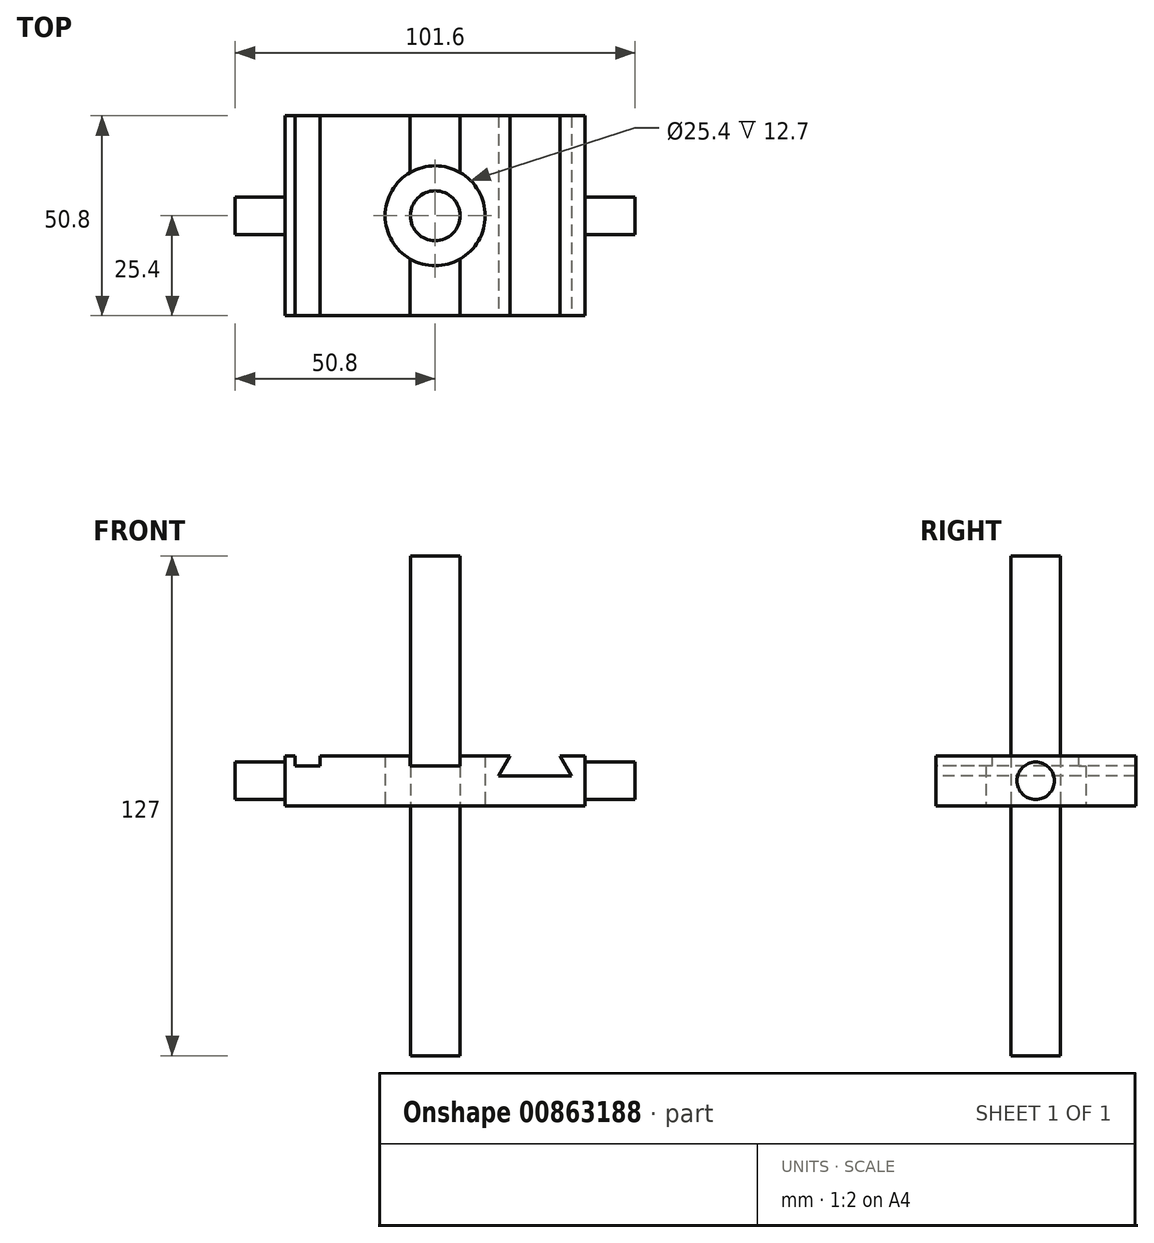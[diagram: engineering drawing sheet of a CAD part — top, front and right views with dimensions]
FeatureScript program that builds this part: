
annotation { "Feature Type Name" : "Feature", "Feature Type Description" : "" }
export const myFeature = defineFeature(function(context is Context, id is Id, definition is map)
    precondition{}
    {
        {
            var Q0;
            Q0=qCreatedBy(makeId("Top.planeOp"),FACE);
            var sketch = newSketch(context, id + "F0", { "sketchPlane" : qUnion([Q0])});
            skLineSegment(sketch, "E0.bottom", {"start": v(38.1, 25.4) * mm, "end": v(-38.1, 25.4) * mm});
            skLineSegment(sketch, "E0.top", {"start": v(38.1, -25.4) * mm, "end": v(-38.1, -25.4) * mm});
            skLineSegment(sketch, "E0.left", {"start": v(38.1, 25.4) * mm, "end": v(38.1, -25.4) * mm});
            skLineSegment(sketch, "E0.right", {"start": v(-38.1, 25.4) * mm, "end": v(-38.1, -25.4) * mm});
            skPoint(sketch, "E0.middle", {"position": v(0, 0) * mm});
            skCircle(sketch, "E1", {"center": v(0, 0) * mm, "radius": 12.7 * mm});
            skSolve(sketch);
        }
        {
            var Q0;
            Q0=makeQuery(id+"F0.imprint","IMPRINT",FACE,{"disambiguationData":[TD([[makeQuery(id+"F0.imprint","IMPRINT",EDGE,{"derivedFrom":sQuery(id+"F0.wireOp",EDGE,"E0.bottom")}),1.0]])]});
            extrude(context, id + "F1", {"entities" : qUnion([Q0]), "depth" : 12.7 * mm, "offsetDistance" : 25.4 * mm});
        }
        {
            var Q0;
            Q0=makeQuery(id+"F1.opExtrude","CAP_FACE",FACE,{"disambiguationData":[OSD([sQuery(id+"F0.wireOp",EDGE,"E0.bottom"),sQuery(id+"F0.wireOp",EDGE,"E0.top"),sQuery(id+"F0.wireOp",EDGE,"E0.left"),sQuery(id+"F0.wireOp",EDGE,"E0.right"),sQuery(id+"F0.wireOp",EDGE,"E1")])],"isStart":false});
            var sketch = newSketch(context, id + "F2", { "sketchPlane" : qUnion([Q0])});
            skLineSegment(sketch, "E2.bottom", {"start": v(-35.56, 25.4) * mm, "end": v(-29.21, 25.4) * mm});
            skLineSegment(sketch, "E2.top", {"start": v(-35.56, -25.4) * mm, "end": v(-29.21, -25.4) * mm});
            skLineSegment(sketch, "E2.left", {"start": v(-35.56, 25.4) * mm, "end": v(-35.56, -25.4) * mm});
            skLineSegment(sketch, "E2.right", {"start": v(-29.21, 25.4) * mm, "end": v(-29.21, -25.4) * mm});
            skLineSegment(sketch, "E3", {"start": v(-6.35, 25.4) * mm, "end": v(-6.35, -25.4) * mm});
            skLineSegment(sketch, "E4", {"start": v(-6.35, -25.4) * mm, "end": v(6.35, -25.4) * mm});
            skLineSegment(sketch, "E5", {"start": v(6.35, -25.4) * mm, "end": v(6.35, 25.4) * mm});
            skLineSegment(sketch, "E6", {"start": v(6.35, 25.4) * mm, "end": v(-6.35, 25.4) * mm});
            skPoint(sketch, "E7", {"position": v(0, 0) * mm});
            skLineSegment(sketch, "E8", {"start": v(0, 25.4) * mm, "end": v(0, -25.4) * mm, "construction": true});
            skSolve(sketch);
        }
        {
            var Q0;
            Q0=makeQuery(id+"F2.imprint","IMPRINT",FACE,{"disambiguationData":[TD([[makeQuery(id+"F2.imprint","IMPRINT",EDGE,{"derivedFrom":sQuery(id+"F2.wireOp",EDGE,"E2.bottom")}),1.0]])]});
            var Q1;
            {var subQ0=sQuery(id+"F2.wireOp",EDGE,"E6");Q1=makeQuery(id+"F2.imprint","IMPRINT",FACE,{"disambiguationData":[TD([[makeQuery(id+"F2.imprint","IMPRINT",EDGE,{"derivedFrom":subQ0}),1.0]])]});}
            var Q2;
            {var subQ0=sQuery(id+"F2.wireOp",EDGE,"E4");Q2=makeQuery(id+"F2.imprint","IMPRINT",FACE,{"disambiguationData":[TD([[makeQuery(id+"F2.imprint","IMPRINT",EDGE,{"derivedFrom":subQ0}),-1.0]])]});}
            extrude(context, id + "F3", {"entities" : qUnion([Q0, Q1, Q2]), "operationType" : NewBodyOperationType.REMOVE, "oppositeDirection" : true, "depth" : 2.54 * mm, "offsetDistance" : 25.4 * mm});
        }
        {
            var Q0;
            Q0=makeQuery(id+"F1.opExtrude","SWEPT_FACE",FACE,{"disambiguationData":[OSD([sQuery(id+"F0.wireOp",EDGE,"E0.top")])]});
            var sketch = newSketch(context, id + "F4", { "sketchPlane" : qUnion([Q0])});
            skLineSegment(sketch, "E9", {"start": v(19.05, 12.7) * mm, "end": v(16.12, 7.62) * mm});
            skLineSegment(sketch, "E10", {"start": v(16.12, 7.62) * mm, "end": v(34.68, 7.62) * mm});
            skLineSegment(sketch, "E11", {"start": v(34.68, 7.62) * mm, "end": v(31.75, 12.7) * mm});
            skLineSegment(sketch, "E12", {"start": v(19.05, 12.7) * mm, "end": v(31.75, 12.7) * mm, "construction": true});
            skLineSegment(sketch, "E13", {"start": v(25.4, 12.7) * mm, "end": v(25.4, 7.62) * mm, "construction": true});
            skSolve(sketch);
        }
        {
            var Q0;
            {var subQ0=sQuery(id+"F4.wireOp",EDGE,"E9");Q0=makeQuery(id+"F4.imprint","IMPRINT",FACE,{"disambiguationData":[TD([[makeQuery(id+"F4.imprint","IMPRINT",EDGE,{"derivedFrom":subQ0}),1.0]])]});}
            extrude(context, id + "F5", {"entities" : qUnion([Q0]), "operationType" : NewBodyOperationType.REMOVE, "endBound" : BoundingType.THROUGH_ALL, "oppositeDirection" : true, "depth" : 25.4 * mm, "offsetDistance" : 25.4 * mm});
        }
        {
            var Q0;
            Q0=makeQuery(id+"F1.opExtrude","SWEPT_FACE",FACE,{"disambiguationData":[OSD([sQuery(id+"F0.wireOp",EDGE,"E0.left")])]});
            var sketch = newSketch(context, id + "F6", { "sketchPlane" : qUnion([Q0])});
            skLineSegment(sketch, "E14", {"start": v(-25.4, 6.35) * mm, "end": v(25.4, 6.35) * mm, "construction": true});
            skLineSegment(sketch, "E15", {"start": v(0, 12.7) * mm, "end": v(0, 0) * mm, "construction": true});
            skCircle(sketch, "E16", {"center": v(0, 6.35) * mm, "radius": 4.76 * mm});
            skSolve(sketch);
        }
        {
            var Q0;
            Q0=makeQuery(id+"F6.imprint","IMPRINT",FACE,{"disambiguationData":[TD([[makeQuery(id+"F6.imprint","IMPRINT",EDGE,{"derivedFrom":sQuery(id+"F6.wireOp",EDGE,"E16")}),1.0]])]});
            extrude(context, id + "F7", {"entities" : qUnion([Q0]), "operationType" : NewBodyOperationType.ADD, "depth" : 12.7 * mm, "offsetDistance" : 25.4 * mm});
        }
        {
            var Q0;
            Q0=qCreatedBy(makeId("Top.planeOp"),FACE);
            var sketch = newSketch(context, id + "F8", { "sketchPlane" : qUnion([Q0])});
            skCircle(sketch, "E17", {"center": v(0, 0) * mm, "radius": 6.32 * mm});
            skSolve(sketch);
        }
        {
            var Q0;
            Q0 = qSketchRegion(id + "F8", true);
            extrude(context, id + "F9", {"entities" : qUnion([Q0]), "endBound" : BoundingType.SYMMETRIC, "depth" : 127 * mm, "offsetDistance" : 25.4 * mm});
        }
        {
            var Q0;
            Q0=makeQuery(id+"F1.opExtrude","SWEPT_FACE",FACE,{"disambiguationData":[OSD([sQuery(id+"F0.wireOp",EDGE,"E0.right")])]});
            var sketch = newSketch(context, id + "F10", { "sketchPlane" : qUnion([Q0])});
            skLineSegment(sketch, "E18", {"start": v(-25.4, 6.35) * mm, "end": v(25.4, 6.35) * mm, "construction": true});
            skLineSegment(sketch, "E19", {"start": v(0, 12.7) * mm, "end": v(0, 0) * mm, "construction": true});
            skCircle(sketch, "E20", {"center": v(0, 6.35) * mm, "radius": 4.76 * mm});
            skSolve(sketch);
        }
        {
            var Q0;
            Q0 = qSketchRegion(id + "F10", true);
            extrude(context, id + "F11", {"entities" : qUnion([Q0]), "operationType" : NewBodyOperationType.ADD, "depth" : 12.7 * mm, "offsetDistance" : 25.4 * mm});
        }
    });
